# Revit family: EL_Galaxy_v2
name_source: partatom
category: Lighting Fixtures
units: mm (PartAtom-declared; Revit-internal decimal feet)

## family parameters
Always vertical = Yes
Cut with Voids When Loaded = No
Light Source = Yes
Maintain Annotation Orientation = No
OmniClass Number = 23.80.70.00
OmniClass Title = Lighting
Part Type = Normal
Room Calculation Point = No
Round Connector Dimension = Use Diameter
Shared = No
Work Plane-Based = No

## types (70) — shared parameters
CE Conformity = CE Mark
CRI = 70
Certification = ENEC, ENEC+, EMC, Zhaga D4i, IDA
Color Filter = 16777215
Control Gear = LED Driver
Default Elevation = 1500 mm  [stored 4.92126 ft]
Description = Street luminaire
Diffuser Material  = Flat glass
Dimming Lamp Color Temperature Shift = <None>
EL_Voltage = AC 220V - 240V / 50-60Hz
Emit from Line Length = 610 mm
Housing Height = 407 mm  [stored 1.3353 ft]
Housing Length = 841 mm
Housing Width = 321 mm  [stored 1.05315 ft]
IK = IK09
IP = IP66
Lamp = LED
Life Time = 100 000 h
Light Source Symbol Length = 3048 mm  [stored 10 ft]
Luminaire Material = Kov
Manufacturer = ELEKTRO-LUMEN, s. r. o.
Spot Beam Angle = 30.00°
Spot Field Angle = 90.00°
Terminal Block Poles = 2, 3, 5
Tilt Angle = 90.00°
URL Luminaire = https://www.el-lumen.cz
URL Manufacturer = https://www.el-lumen.cz
Voltage  = AC 220V - 240V / 50-60Hz
Weight = 10

## per-type parameters (varying)
| type | CCT | Galaxy A | Galaxy S | Luminaire Type | Luminous Flux of LED | Luminous Flux of Luminaire | Model | Optic | Optical Efficacy | Power |
| GALAXY A4  Mxx 10k0 740 | 4000 | Yes | No | GALAXY A4 | 10000 lm | 6340 lm | GALAXY A4 | M03 | 63.4 | 53 W |
| GALAXY A4  Mxx 9k0 740 | 4000 | Yes | No | GALAXY A4 | 9000 lm | 5706 lm | GALAXY A4 | M03 | 63.4 | 47 W |
| GALAXY A4  Mxx 8k0 740 | 4000 | Yes | No | GALAXY A4 | 8000 lm | 5072 lm | GALAXY A4 | M03 | 63.4 | 42 W |
| GALAXY A4  Mxx 7k0 740 | 4000 | Yes | No | GALAXY A4 | 7000 lm | 4438 lm | GALAXY A4 | M03 | 63.4 | 37 W |
| GALAXY A4  Mxx 6k0 740 | 4000 | Yes | No | GALAXY A4 | 6000 lm | 3804 lm | GALAXY A4 | M03 | 63.4 | 32 W |
| GALAXY A4  Mxx 5k0 740 | 4000 | Yes | No | GALAXY A4 | 5000 lm | 3170 lm | GALAXY A4 | M03 | 63.4 | 26 W |
| GALAXY A4  Mxx 4k0 740 | 4000 | Yes | No | GALAXY A4 | 4000 lm | 2536 lm | GALAXY A4 | M03 | 63.4 | 21 W |
| GALAXY A4  Mxx 3k0 740 | 4000 | Yes | No | GALAXY A4 | 3000 lm | 1902 lm | GALAXY A4 | M03 | 63.4 | 15 W |
| GALAXY A4  Mxx 2k0 740 | 4000 | Yes | No | GALAXY A4 | 2000 lm | 1268 lm | GALAXY A4 | M03 | 63.4 | 10 W |
| GALAXY A4  Mxx 10k0 730 | 3000 | Yes | No | GALAXY A4 | 10000 lm | 6340 lm | GALAXY A4 | M03 | 63.4 | 56 W |
| GALAXY A4  Mxx 9k0 730 | 3000 | Yes | No | GALAXY A4 | 9000 lm | 5706 lm | GALAXY A4 | M03 | 63.4 | 50 W |
| GALAXY A4  Mxx 8k0 730 | 3000 | Yes | No | GALAXY A4 | 8000 lm | 5072 lm | GALAXY A4 | M03 | 63.4 | 45 W |
| GALAXY A4  Mxx 7k0 730 | 3000 | Yes | No | GALAXY A4 | 7000 lm | 4438 lm | GALAXY A4 | M03 | 63.4 | 39 W |
| GALAXY A4  Mxx 6k0 730 | 3000 | Yes | No | GALAXY A4 | 6000 lm | 3804 lm | GALAXY A4 | M03 | 63.4 | 34 W |
| GALAXY A4  Mxx 5k0 730 | 3000 | Yes | No | GALAXY A4 | 5000 lm | 3170 lm | GALAXY A4 | M03 | 63.4 | 28 W |
| GALAXY A4  Mxx 4k0 730 | 3000 | Yes | No | GALAXY A4 | 4000 lm | 2536 lm | GALAXY A4 | M03 | 63.4 | 23 W |
| GALAXY A4  Mxx 3k0 730 | 3000 | Yes | No | GALAXY A4 | 3000 lm | 1902 lm | GALAXY A4 | M03 | 63.4 | 17 W |
| GALAXY A4  Mxx 2k0 730 | 3000 | Yes | No | GALAXY A4 | 2000 lm | 1268 lm | GALAXY A4 | M03 | 63.4 | 11 W |
| GALAXY A4  Mxx 10k0 727 | 2700 | Yes | No | GALAXY A4 | 10000 lm | 6340 lm | GALAXY A4 | M03 | 63.4 | 59 W |
| GALAXY A4  Mxx 9k0 727 | 2700 | Yes | No | GALAXY A4 | 9000 lm | 5706 lm | GALAXY A4 | M03 | 63.4 | 53 W |
| GALAXY A4  Mxx 8k0 727 | 2700 | Yes | No | GALAXY A4 | 8000 lm | 5072 lm | GALAXY A4 | M03 | 63.4 | 47 W |
| GALAXY A4  Mxx 7k0 727 | 2700 | Yes | No | GALAXY A4 | 7000 lm | 4438 lm | GALAXY A4 | M03 | 63.4 | 42 W |
| GALAXY A4  Mxx 6k0 727 | 2700 | Yes | No | GALAXY A4 | 6000 lm | 3804 lm | GALAXY A4 | M03 | 63.4 | 35 W |
| GALAXY A4  Mxx 5k0 727 | 2700 | Yes | No | GALAXY A4 | 5000 lm | 3170 lm | GALAXY A4 | M03 | 63.4 | 29 W |
| GALAXY A4  Mxx 4k0 727 | 2700 | Yes | No | GALAXY A4 | 4000 lm | 2536 lm | GALAXY A4 | M03 | 63.4 | 24 W |
| GALAXY A4  Mxx 3k0 727 | 2700 | Yes | No | GALAXY A4 | 3000 lm | 1902 lm | GALAXY A4 | M03 | 63.4 | 18 W |
| GALAXY A4  Mxx 2k0 727 | 2700 | Yes | No | GALAXY A4 | 2000 lm | 1268 lm | GALAXY A4 | M03 | 63.4 | 12 W |
| GALAXY A4  Mxx 9k0 722 | 2200 | Yes | No | GALAXY A4 | 9000 lm | 5706 lm | GALAXY A4 | M03 | 63.4 | 60 W |
| GALAXY A4  Mxx 8k0 722 | 2200 | Yes | No | GALAXY A4 | 8000 lm | 5072 lm | GALAXY A4 | M03 | 63.4 | 53 W |
| GALAXY A4  Mxx 7k0 722 | 2200 | Yes | No | GALAXY A4 | 7000 lm | 4438 lm | GALAXY A4 | M03 | 63.4 | 46 W |
| GALAXY A4  Mxx 6k0 722 | 2200 | Yes | No | GALAXY A4 | 6000 lm | 3804 lm | GALAXY A4 | M03 | 63.4 | 40 W |
| GALAXY A4  Mxx 5k0 722 | 2200 | Yes | No | GALAXY A4 | 5000 lm | 3170 lm | GALAXY A4 | M03 | 63.4 | 33 W |
| GALAXY A4  Mxx 4k0 722 | 2200 | Yes | No | GALAXY A4 | 4000 lm | 2536 lm | GALAXY A4 | M03 | 63.4 | 27 W |
| GALAXY A4  Mxx 3k0 722 | 2200 | Yes | No | GALAXY A4 | 3000 lm | 1902 lm | GALAXY A4 | M03 | 63.4 | 20 W |
| GALAXY A4  Mxx 2k0 722 | 2200 | Yes | No | GALAXY A4 | 2000 lm | 1268 lm | GALAXY A4 | M03 | 63.4 | 13 W |
| GALAXY S4  Mxx 10k0 740 | 4000 | No | Yes | GALAXY S4 | 10000 lm | 6437 lm | GALAXY S4 | U02 | 64.37 | 53 W |
| GALAXY S4  Mxx 9k0 740 | 4000 | No | Yes | GALAXY S4 | 9000 lm | 5793 lm | GALAXY S4 | U02 | 64.37 | 47 W |
| GALAXY S4  Mxx 8k0 740 | 4000 | No | Yes | GALAXY S4 | 8000 lm | 5150 lm | GALAXY S4 | U02 | 64.37 | 42 W |
| GALAXY S4  Mxx 7k0 740 | 4000 | No | Yes | GALAXY S4 | 7000 lm | 4506 lm | GALAXY S4 | U02 | 64.37 | 37 W |
| GALAXY S4  Mxx 6k0 740 | 4000 | No | Yes | GALAXY S4 | 6000 lm | 3862 lm | GALAXY S4 | U02 | 64.37 | 32 W |
| GALAXY S4  Mxx 5k0 740 | 4000 | No | Yes | GALAXY S4 | 5000 lm | 3219 lm | GALAXY S4 | U02 | 64.37 | 26 W |
| GALAXY S4  Mxx 4k0 740 | 4000 | No | Yes | GALAXY S4 | 4000 lm | 2575 lm | GALAXY S4 | U02 | 64.37 | 21 W |
| GALAXY S4  Mxx 3k0 740 | 4000 | No | Yes | GALAXY S4 | 3000 lm | 1931 lm | GALAXY S4 | U02 | 64.37 | 15 W |
| GALAXY S4  Mxx 2k0 740 | 4000 | No | Yes | GALAXY S4 | 2000 lm | 1287 lm | GALAXY S4 | U02 | 64.37 | 10 W |
| GALAXY S4  Mxx 10k0 730 | 3000 | No | Yes | GALAXY S4 | 10000 lm | 6437 lm | GALAXY S4 | U02 | 64.37 | 56 W |
| GALAXY S4  Mxx 9k0 730 | 3000 | No | Yes | GALAXY S4 | 9000 lm | 5793 lm | GALAXY S4 | U02 | 64.37 | 50 W |
| GALAXY S4  Mxx 8k0 730 | 3000 | No | Yes | GALAXY S4 | 8000 lm | 5150 lm | GALAXY S4 | U02 | 64.37 | 45 W |
| GALAXY S4  Mxx 7k0 730 | 3000 | No | Yes | GALAXY S4 | 7000 lm | 4506 lm | GALAXY S4 | U02 | 64.37 | 39 W |
| GALAXY S4  Mxx 6k0 730 | 3000 | No | Yes | GALAXY S4 | 6000 lm | 3862 lm | GALAXY S4 | U02 | 64.37 | 34 W |
| GALAXY S4  Mxx 5k0 730 | 3000 | No | Yes | GALAXY S4 | 5000 lm | 3219 lm | GALAXY S4 | U02 | 64.37 | 28 W |
| GALAXY S4  Mxx 4k0 730 | 3000 | No | Yes | GALAXY S4 | 4000 lm | 2575 lm | GALAXY S4 | U02 | 64.37 | 23 W |
| GALAXY S4  Mxx 3k0 730 | 3000 | No | Yes | GALAXY S4 | 3000 lm | 1931 lm | GALAXY S4 | U02 | 64.37 | 17 W |
| GALAXY S4  Mxx 2k0 730 | 3000 | No | Yes | GALAXY S4 | 2000 lm | 1287 lm | GALAXY S4 | U02 | 64.37 | 11 W |
| GALAXY S4  Mxx 10k0 727 | 2700 | No | Yes | GALAXY S4 | 10000 lm | 6437 lm | GALAXY S4 | U02 | 64.37 | 59 W |
| GALAXY S4  Mxx 9k0 727 | 2700 | No | Yes | GALAXY S4 | 9000 lm | 5793 lm | GALAXY S4 | U02 | 64.37 | 53 W |
| GALAXY S4  Mxx 8k0 727 | 2700 | No | Yes | GALAXY S4 | 8000 lm | 5150 lm | GALAXY S4 | U02 | 64.37 | 47 W |
| GALAXY S4  Mxx 7k0 727 | 2700 | No | Yes | GALAXY S4 | 7000 lm | 4506 lm | GALAXY S4 | U02 | 64.37 | 42 W |
| GALAXY S4  Mxx 6k0 727 | 2700 | No | Yes | GALAXY S4 | 6000 lm | 3862 lm | GALAXY S4 | U02 | 64.37 | 35 W |
| GALAXY S4  Mxx 5k0 727 | 2700 | No | Yes | GALAXY S4 | 5000 lm | 3219 lm | GALAXY S4 | U02 | 64.37 | 29 W |
| GALAXY S4  Mxx 4k0 727 | 2700 | No | Yes | GALAXY S4 | 4000 lm | 2575 lm | GALAXY S4 | U02 | 64.37 | 24 W |
| GALAXY S4  Mxx 3k0 727 | 2700 | No | Yes | GALAXY S4 | 3000 lm | 1931 lm | GALAXY S4 | U02 | 64.37 | 18 W |
| GALAXY S4  Mxx 2k0 727 | 2700 | No | Yes | GALAXY S4 | 2000 lm | 1287 lm | GALAXY S4 | U02 | 64.37 | 12 W |
| GALAXY S4  Mxx 9k0 722 | 2200 | No | Yes | GALAXY S4 | 9000 lm | 5793 lm | GALAXY S4 | U02 | 64.37 | 60 W |
| GALAXY S4  Mxx 8k0 722 | 2200 | No | Yes | GALAXY S4 | 8000 lm | 5150 lm | GALAXY S4 | U02 | 64.37 | 53 W |
| GALAXY S4  Mxx 7k0 722 | 2200 | No | Yes | GALAXY S4 | 7000 lm | 4506 lm | GALAXY S4 | U02 | 64.37 | 46 W |
| GALAXY S4  Mxx 6k0 722 | 2200 | No | Yes | GALAXY S4 | 6000 lm | 3862 lm | GALAXY S4 | U02 | 64.37 | 40 W |
| GALAXY S4  Mxx 5k0 722 | 2200 | No | Yes | GALAXY S4 | 5000 lm | 3219 lm | GALAXY S4 | U02 | 64.37 | 33 W |
| GALAXY S4  Mxx 4k0 722 | 2200 | No | Yes | GALAXY S4 | 4000 lm | 2575 lm | GALAXY S4 | U02 | 64.37 | 27 W |
| GALAXY S4  Mxx 3k0 722 | 2200 | No | Yes | GALAXY S4 | 3000 lm | 1931 lm | GALAXY S4 | U02 | 64.37 | 20 W |
| GALAXY S4  Mxx 2k0 722 | 2200 | No | Yes | GALAXY S4 | 2000 lm | 1287 lm | GALAXY S4 | U02 | 64.37 | 13 W |

note: column(s) folded — value = type name in every type: Luminaire Model

note: [stored X ft] marks values corroborated as IEEE doubles in the binary element streams (Revit-internal decimal feet)
